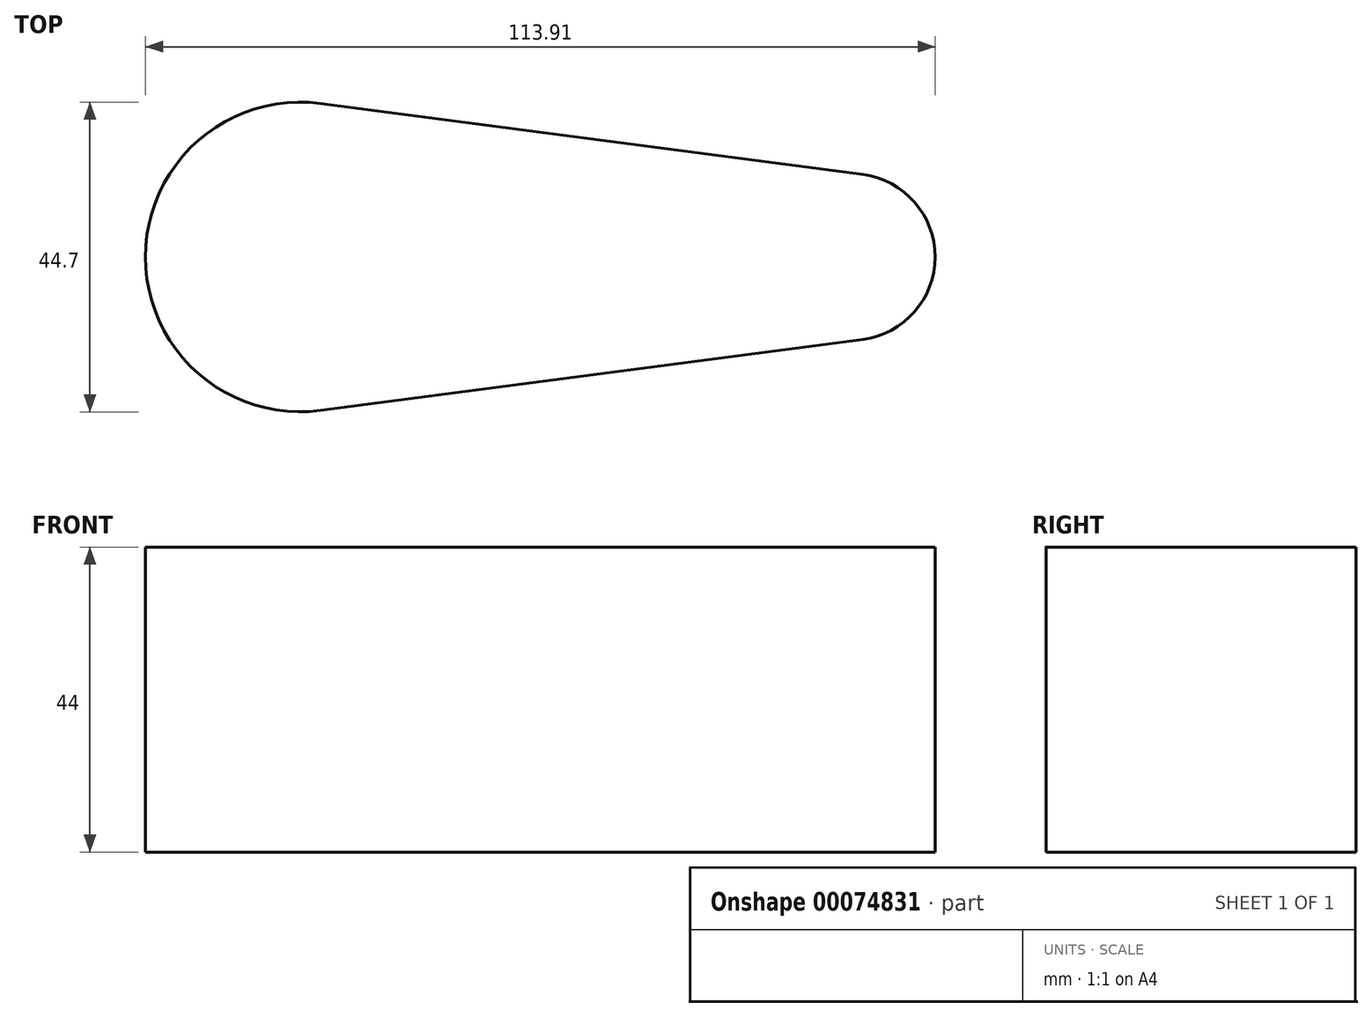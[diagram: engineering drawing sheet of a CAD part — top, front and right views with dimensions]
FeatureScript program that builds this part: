
annotation { "Feature Type Name" : "Feature", "Feature Type Description" : "" }
export const myFeature = defineFeature(function(context is Context, id is Id, definition is map)
    precondition{}
    {
        {
            var Q0;
            Q0=qCreatedBy(makeId("Top.planeOp"),FACE);
            var sketch = newSketch(context, id + "F0", { "sketchPlane" : qUnion([Q0])});
            skArc(sketch, "E0", {"start": v(-37.7, 22.16) * mm, "mid": v(-55.35, 16.8) * mm, "end": v(-62.95, 0) * mm});
            skArc(sketch, "E1.MirrorCS", {"start": v(-37.7, -22.16) * mm, "mid": v(-55.35, -16.8) * mm, "end": v(-62.95, 0) * mm});
            skArc(sketch, "E2", {"start": v(40.52, 11.9) * mm, "mid": v(47.98, 7.91) * mm, "end": v(50.96, 0) * mm});
            skArc(sketch, "E3.MirrorCS", {"start": v(40.52, -11.9) * mm, "mid": v(47.98, -7.91) * mm, "end": v(50.96, 0) * mm});
            skLineSegment(sketch, "E4", {"start": v(-37.7, -22.16) * mm, "end": v(40.52, -11.9) * mm});
            skLineSegment(sketch, "E5", {"start": v(-37.7, 22.16) * mm, "end": v(40.52, 11.9) * mm});
            skSolve(sketch);
        }
        {
            var Q0;
            Q0 = qSketchRegion(id + "F0", true);
            extrude(context, id + "F1", {"entities" : qUnion([Q0]), "depth" : 44 * mm});
        }
    });
